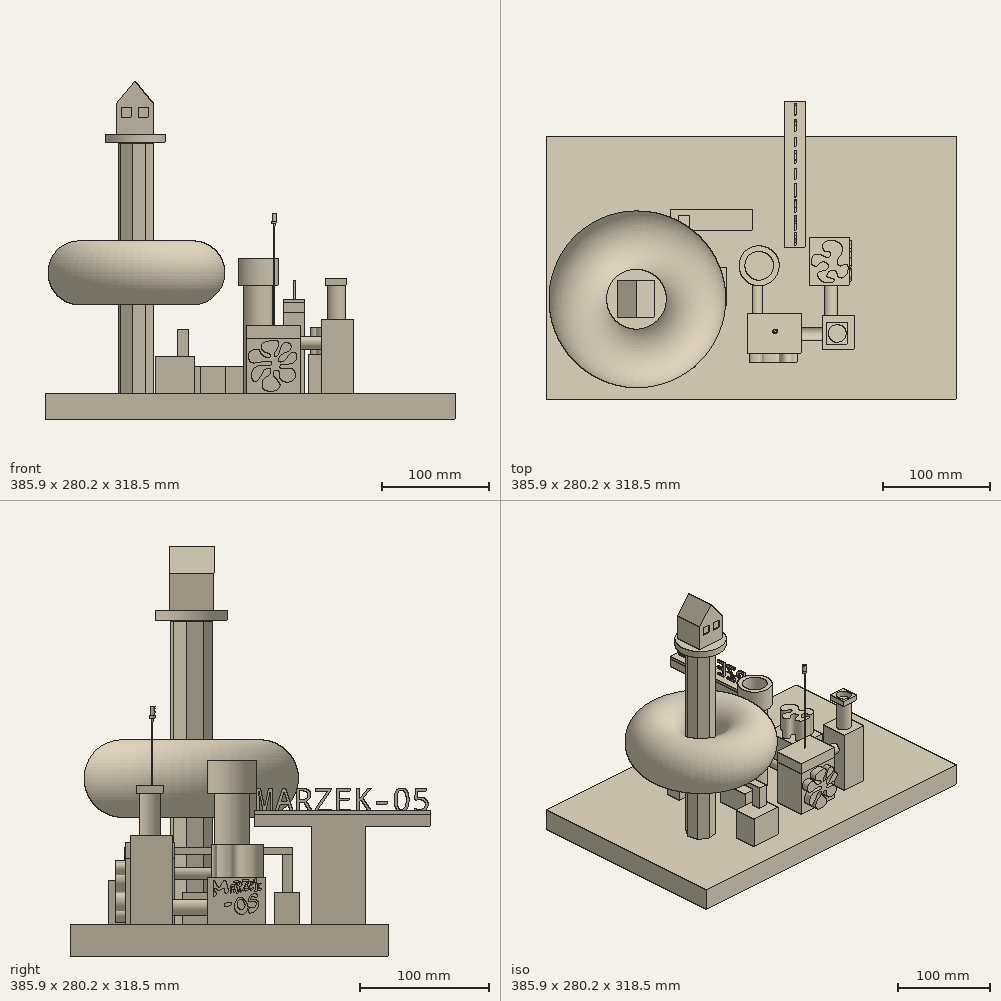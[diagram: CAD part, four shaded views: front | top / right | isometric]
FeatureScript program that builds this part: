
annotation { "Feature Type Name" : "Feature", "Feature Type Description" : "" }
export const myFeature = defineFeature(function(context is Context, id is Id, definition is map)
    precondition{}
    {
        {
            var Q0;
            Q0=qCreatedBy(makeId("Top.planeOp"),FACE);
            var sketch = newSketch(context, id + "F0", { "sketchPlane" : qUnion([Q0])});
            skLineSegment(sketch, "E0.bottom", {"start": v(-130.02, -36.2) * mm, "end": v(-92.83, -36.2) * mm});
            skLineSegment(sketch, "E0.top", {"start": v(-130.02, -64.13) * mm, "end": v(-92.83, -64.13) * mm});
            skLineSegment(sketch, "E0.left", {"start": v(-130.02, -36.2) * mm, "end": v(-130.02, -64.13) * mm});
            skLineSegment(sketch, "E0.right", {"start": v(-92.83, -36.2) * mm, "end": v(-92.83, -64.13) * mm});
            skSolve(sketch);
        }
        {
            var Q0;
            Q0 = qSketchRegion(id + "F0", true);
            extrude(context, id + "F1", {"entities" : qUnion([Q0]), "depth" : 34.54 * mm, "offsetDistance" : 25.4 * mm});
        }
        {
            var Q0;
            Q0=qCreatedBy(makeId("Top.planeOp"),FACE);
            var sketch = newSketch(context, id + "F2", { "sketchPlane" : qUnion([Q0])});
            skLineSegment(sketch, "E1.bottom", {"start": v(-87.23, -7.14) * mm, "end": v(-63.83, -7.14) * mm});
            skLineSegment(sketch, "E1.top", {"start": v(-87.23, 30.34) * mm, "end": v(-63.83, 30.34) * mm});
            skLineSegment(sketch, "E1.left", {"start": v(-87.23, -7.14) * mm, "end": v(-87.23, 30.34) * mm});
            skLineSegment(sketch, "E1.right", {"start": v(-63.83, -7.14) * mm, "end": v(-63.83, 30.34) * mm});
            skSolve(sketch);
        }
        {
            var Q0;
            Q0 = qSketchRegion(id + "F2", true);
            extrude(context, id + "F3", {"entities" : qUnion([Q0]), "depth" : 25.4 * mm, "offsetDistance" : 25.4 * mm});
        }
        {
            var Q0;
            Q0=qCreatedBy(makeId("Top.planeOp"),FACE);
            var sketch = newSketch(context, id + "F4", { "sketchPlane" : qUnion([Q0])});
            skLineSegment(sketch, "E2.bottom", {"start": v(-44.01, -13.42) * mm, "end": v(6.45, -13.42) * mm});
            skLineSegment(sketch, "E2.top", {"start": v(-44.01, -51.12) * mm, "end": v(6.45, -51.12) * mm});
            skLineSegment(sketch, "E2.left", {"start": v(-44.01, -13.42) * mm, "end": v(-44.01, -51.12) * mm});
            skLineSegment(sketch, "E2.right", {"start": v(6.45, -13.42) * mm, "end": v(6.45, -51.12) * mm});
            skSolve(sketch);
        }
        {
            var Q0;
            Q0 = qSketchRegion(id + "F4", true);
            extrude(context, id + "F5", {"entities" : qUnion([Q0]), "depth" : 51.56 * mm, "offsetDistance" : 25.4 * mm});
        }
        {
            var Q0;
            Q0=qCreatedBy(makeId("Top.planeOp"),FACE);
            var sketch = newSketch(context, id + "F6", { "sketchPlane" : qUnion([Q0])});
            skLineSegment(sketch, "E3.bottom", {"start": v(51.77, 57.86) * mm, "end": v(13.62, 57.86) * mm});
            skLineSegment(sketch, "E3.top", {"start": v(51.77, 12.59) * mm, "end": v(13.62, 12.59) * mm});
            skLineSegment(sketch, "E3.left", {"start": v(51.77, 57.86) * mm, "end": v(51.77, 12.59) * mm});
            skLineSegment(sketch, "E3.right", {"start": v(13.62, 57.86) * mm, "end": v(13.62, 12.59) * mm});
            skSolve(sketch);
        }
        {
            var Q0;
            Q0 = qSketchRegion(id + "F6", true);
            extrude(context, id + "F7", {"entities" : qUnion([Q0]), "depth" : 36.58 * mm, "offsetDistance" : 25.4 * mm});
        }
        {
            var Q0;
            Q0=qCreatedBy(makeId("Top.planeOp"),FACE);
            var sketch = newSketch(context, id + "F8", { "sketchPlane" : qUnion([Q0])});
            skLineSegment(sketch, "E4.bottom", {"start": v(-116.39, 64.97) * mm, "end": v(-39.84, 64.97) * mm});
            skLineSegment(sketch, "E4.top", {"start": v(-116.39, 84.23) * mm, "end": v(-39.84, 84.23) * mm});
            skLineSegment(sketch, "E4.left", {"start": v(-116.39, 64.97) * mm, "end": v(-116.39, 84.23) * mm});
            skLineSegment(sketch, "E4.right", {"start": v(-39.84, 64.97) * mm, "end": v(-39.84, 84.23) * mm});
            skSolve(sketch);
        }
        {
            var Q0;
            Q0 = qSketchRegion(id + "F8", true);
            extrude(context, id + "F9", {"entities" : qUnion([Q0]), "depth" : 25.4 * mm, "offsetDistance" : 25.4 * mm});
        }
        {
            var Q0;
            Q0=qCreatedBy(makeId("Top.planeOp"),FACE);
            var sketch = newSketch(context, id + "F10", { "sketchPlane" : qUnion([Q0])});
            skCircle(sketch, "E5", {"center": v(-33.26, 31.48) * mm, "radius": 13.51 * mm});
            skSolve(sketch);
        }
        {
            var Q0;
            Q0 = qSketchRegion(id + "F10", true);
            extrude(context, id + "F11", {"entities" : qUnion([Q0]), "depth" : 101.85 * mm, "offsetDistance" : 25.4 * mm});
        }
        {
            var Q0;
            Q0=qCreatedBy(makeId("Top.planeOp"),FACE);
            var sketch = newSketch(context, id + "F12", { "sketchPlane" : qUnion([Q0])});
            skLineSegment(sketch, "E6.bottom", {"start": v(56.17, -47.26) * mm, "end": v(26.64, -47.26) * mm});
            skLineSegment(sketch, "E6.top", {"start": v(56.17, -14.92) * mm, "end": v(26.64, -14.92) * mm});
            skLineSegment(sketch, "E6.left", {"start": v(56.17, -47.26) * mm, "end": v(56.17, -14.92) * mm});
            skLineSegment(sketch, "E6.right", {"start": v(26.64, -47.26) * mm, "end": v(26.64, -14.92) * mm});
            skSolve(sketch);
        }
        {
            var Q0;
            Q0 = qSketchRegion(id + "F12", true);
            extrude(context, id + "F13", {"entities" : qUnion([Q0]), "depth" : 69.6 * mm, "offsetDistance" : 25.4 * mm});
        }
        {
            var Q0;
            Q0=makeQuery(id+"F13.opExtrude","SWEPT_FACE",FACE,{"disambiguationData":[OSD([sQuery(id+"F12.wireOp",EDGE,"E6.top")])]});
            var sketch = newSketch(context, id + "F14", { "sketchPlane" : qUnion([Q0])});
            skCircle(sketch, "E7", {"center": v(-34.44, 13.3) * mm, "radius": 6.1 * mm});
            skSolve(sketch);
        }
        {
            var Q0;
            Q0 = qSketchRegion(id + "F14", true);
            extrude(context, id + "F15", {"entities" : qUnion([Q0]), "depth" : 30.99 * mm, "offsetDistance" : 25.4 * mm});
        }
        {
            var Q0;
            Q0=makeQuery(id+"F13.opExtrude","SWEPT_FACE",FACE,{"disambiguationData":[OSD([sQuery(id+"F12.wireOp",EDGE,"E6.right")])]});
            var sketch = newSketch(context, id + "F16", { "sketchPlane" : qUnion([Q0])});
            skCircle(sketch, "E8", {"center": v(32.58, 47.44) * mm, "radius": 6.12 * mm});
            skSolve(sketch);
        }
        {
            var Q0;
            Q0 = qSketchRegion(id + "F16", true);
            extrude(context, id + "F17", {"entities" : qUnion([Q0]), "depth" : 25.4 * mm, "offsetDistance" : 25.4 * mm});
        }
        {
            var Q0;
            Q0=makeQuery(id+"F5.opExtrude","CAP_FACE",FACE,{"disambiguationData":[OSD([sQuery(id+"F4.wireOp",EDGE,"E2.bottom"),sQuery(id+"F4.wireOp",EDGE,"E2.top"),sQuery(id+"F4.wireOp",EDGE,"E2.left"),sQuery(id+"F4.wireOp",EDGE,"E2.right")])],"isStart":false});
            extrude(context, id + "F18", {"entities" : qUnion([Q0]), "depth" : 12.7 * mm, "offsetDistance" : 25.4 * mm});
        }
        {
            var Q0;
            Q0=makeQuery(id+"F5.opExtrude","SWEPT_FACE",FACE,{"disambiguationData":[OSD([sQuery(id+"F4.wireOp",EDGE,"E2.bottom")])]});
            var sketch = newSketch(context, id + "F19", { "sketchPlane" : qUnion([Q0])});
            skCircle(sketch, "E9", {"center": v(35.14, 39.92) * mm, "radius": 4.9 * mm});
            skSolve(sketch);
        }
        {
            var Q0;
            Q0 = qSketchRegion(id + "F19", true);
            extrude(context, id + "F20", {"entities" : qUnion([Q0]), "depth" : 37.85 * mm, "offsetDistance" : 25.4 * mm});
        }
        {
            var Q0;
            Q0=makeQuery(id+"F1.opExtrude","CAP_FACE",FACE,{"disambiguationData":[OSD([sQuery(id+"F0.wireOp",EDGE,"E0.bottom"),sQuery(id+"F0.wireOp",EDGE,"E0.top"),sQuery(id+"F0.wireOp",EDGE,"E0.left"),sQuery(id+"F0.wireOp",EDGE,"E0.right")])],"isStart":false});
            var sketch = newSketch(context, id + "F21", { "sketchPlane" : qUnion([Q0])});
            skLineSegment(sketch, "E10.bottom", {"start": v(-98.59, -40.36) * mm, "end": v(-108.85, -40.36) * mm});
            skLineSegment(sketch, "E10.top", {"start": v(-98.59, -51.65) * mm, "end": v(-108.85, -51.65) * mm});
            skLineSegment(sketch, "E10.left", {"start": v(-98.59, -40.36) * mm, "end": v(-98.59, -51.65) * mm});
            skLineSegment(sketch, "E10.right", {"start": v(-108.85, -40.36) * mm, "end": v(-108.85, -51.65) * mm});
            skSolve(sketch);
        }
        {
            var Q0;
            Q0 = qSketchRegion(id + "F21", true);
            extrude(context, id + "F22", {"entities" : qUnion([Q0]), "operationType" : NewBodyOperationType.ADD, "depth" : 25.4 * mm, "offsetDistance" : 25.4 * mm});
        }
        {
            var Q0;
            Q0=makeQuery(id+"F22.opExtrude","SWEPT_FACE",FACE,{"disambiguationData":[OSD([sQuery(id+"F21.wireOp",EDGE,"E10.bottom")])]});
            var sketch = newSketch(context, id + "F23", { "sketchPlane" : qUnion([Q0])});
            skLineSegment(sketch, "E11.bottom", {"start": v(108.85, 59.94) * mm, "end": v(98.59, 59.94) * mm});
            skLineSegment(sketch, "E11.top", {"start": v(108.85, 54.75) * mm, "end": v(98.59, 54.75) * mm});
            skLineSegment(sketch, "E11.left", {"start": v(108.85, 59.94) * mm, "end": v(108.85, 54.75) * mm});
            skLineSegment(sketch, "E11.right", {"start": v(98.59, 59.94) * mm, "end": v(98.59, 54.75) * mm});
            skSolve(sketch);
        }
        {
            var Q0;
            Q0 = qSketchRegion(id + "F23", true);
            extrude(context, id + "F24", {"entities" : qUnion([Q0]), "operationType" : NewBodyOperationType.ADD, "depth" : 118.87 * mm, "offsetDistance" : 25.4 * mm});
        }
        {
            var Q0;
            Q0=makeQuery(id+"F24.opExtrude","SWEPT_FACE",FACE,{"disambiguationData":[OSD([sQuery(id+"F23.wireOp",EDGE,"E11.top")])]});
            var sketch = newSketch(context, id + "F25", { "sketchPlane" : qUnion([Q0])});
            skLineSegment(sketch, "E12.bottom", {"start": v(-108.85, -78.51) * mm, "end": v(-98.59, -78.51) * mm});
            skLineSegment(sketch, "E12.top", {"start": v(-108.85, -71.06) * mm, "end": v(-98.59, -71.06) * mm});
            skLineSegment(sketch, "E12.left", {"start": v(-108.85, -78.51) * mm, "end": v(-108.85, -71.06) * mm});
            skLineSegment(sketch, "E12.right", {"start": v(-98.59, -78.51) * mm, "end": v(-98.59, -71.06) * mm});
            skSolve(sketch);
        }
        {
            var Q0;
            Q0 = qSketchRegion(id + "F25", true);
            extrude(context, id + "F26", {"entities" : qUnion([Q0]), "depth" : 33.78 * mm, "offsetDistance" : 25.4 * mm});
        }
        {
            var Q0;
            Q0=makeQuery(id+"F11.opExtrude","CAP_FACE",FACE,{"disambiguationData":[OSD([sQuery(id+"F10.wireOp",EDGE,"E5")])],"isStart":false});
            var sketch = newSketch(context, id + "F27", { "sketchPlane" : qUnion([Q0])});
            skCircle(sketch, "E13.0", {"center": v(-33.26, 31.48) * mm, "radius": 18.84 * mm});
            skSolve(sketch);
        }
        {
            var Q0;
            Q0=makeQuery(id+"F27.imprint","IMPRINT",FACE,{"disambiguationData":[TD([[makeQuery(id+"F27.imprint","IMPRINT",EDGE,{"derivedFrom":sQuery(id+"F27.wireOp",EDGE,"E13.0")}),1.0]])]});
            extrude(context, id + "F28", {"entities" : qUnion([Q0]), "depth" : 25.4 * mm, "offsetDistance" : 25.4 * mm});
        }
        {
            var Q0;
            Q0=makeQuery(id+"F13.opExtrude","CAP_FACE",FACE,{"disambiguationData":[OSD([sQuery(id+"F12.wireOp",EDGE,"E6.bottom"),sQuery(id+"F12.wireOp",EDGE,"E6.top"),sQuery(id+"F12.wireOp",EDGE,"E6.left"),sQuery(id+"F12.wireOp",EDGE,"E6.right")])],"isStart":false});
            var sketch = newSketch(context, id + "F29", { "sketchPlane" : qUnion([Q0])});
            skCircle(sketch, "E14", {"center": v(40.34, -32.18) * mm, "radius": 8.32 * mm});
            skSolve(sketch);
        }
        {
            var Q0;
            Q0 = qSketchRegion(id + "F29", true);
            extrude(context, id + "F30", {"entities" : qUnion([Q0]), "operationType" : NewBodyOperationType.ADD, "depth" : 25.4 * mm, "offsetDistance" : 25.4 * mm});
        }
        {
            var Q0;
            Q0=makeQuery(id+"F30.opExtrude","CAP_FACE",FACE,{"disambiguationData":[OSD([sQuery(id+"F29.wireOp",EDGE,"E14")])],"isStart":false});
            extrude(context, id + "F31", {"entities" : qUnion([Q0]), "operationType" : NewBodyOperationType.ADD, "depth" : 7.11 * mm, "offsetDistance" : 25.4 * mm});
        }
        {
            var Q0;
            Q0=makeQuery(id+"F31.opExtrude","CAP_FACE",FACE,{"disambiguationData":[OSD([sQuery(id+"F29.wireOp",EDGE,"E14")])],"isStart":false});
            var sketch = newSketch(context, id + "F32", { "sketchPlane" : qUnion([Q0])});
            skLineSegment(sketch, "E15.bottom", {"start": v(50.17, -42.34) * mm, "end": v(30.38, -42.34) * mm});
            skLineSegment(sketch, "E15.top", {"start": v(50.17, -21.75) * mm, "end": v(30.38, -21.75) * mm});
            skLineSegment(sketch, "E15.left", {"start": v(50.17, -42.34) * mm, "end": v(50.17, -21.75) * mm});
            skLineSegment(sketch, "E15.right", {"start": v(30.38, -42.34) * mm, "end": v(30.38, -21.75) * mm});
            skSolve(sketch);
        }
        {
            var Q0;
            Q0=makeQuery(id+"F32.imprint","IMPRINT",FACE,{"disambiguationData":[TD([[makeQuery(id+"F32.imprint","IMPRINT",EDGE,{"derivedFrom":sQuery(id+"F32.wireOp",EDGE,"E15.bottom")}),-1.0]])]});
            extrude(context, id + "F33", {"entities" : qUnion([Q0]), "depth" : 6.43 * mm, "offsetDistance" : 25.4 * mm});
        }
        {
            var Q0;
            Q0=makeQuery(id+"F18.opExtrude","CAP_FACE",FACE,{"disambiguationData":[OSD([sQuery(id+"F4.wireOp",EDGE,"E2.bottom"),sQuery(id+"F4.wireOp",EDGE,"E2.top"),sQuery(id+"F4.wireOp",EDGE,"E2.left"),sQuery(id+"F4.wireOp",EDGE,"E2.right")])],"isStart":false});
            var sketch = newSketch(context, id + "F34", { "sketchPlane" : qUnion([Q0])});
            skCircle(sketch, "E16", {"center": v(-18.17, -30.28) * mm, "radius": 0.48 * mm});
            skSolve(sketch);
        }
        {
            var Q0;
            Q0 = qSketchRegion(id + "F34", true);
            extrude(context, id + "F35", {"entities" : qUnion([Q0]), "operationType" : NewBodyOperationType.ADD, "depth" : 93.22 * mm, "offsetDistance" : 25.4 * mm});
        }
        {
            var Q0;
            Q0=makeQuery(id+"F35.opExtrude","CAP_FACE",FACE,{"disambiguationData":[OSD([sQuery(id+"F34.wireOp",EDGE,"E16")])],"isStart":false});
            var sketch = newSketch(context, id + "F36", { "sketchPlane" : qUnion([Q0])});
            skCircle(sketch, "E17", {"center": v(-18.17, -30.28) * mm, "radius": 0.82 * mm});
            skSolve(sketch);
        }
        {
            var Q0;
            Q0 = qSketchRegion(id + "F36", true);
            extrude(context, id + "F37", {"entities" : qUnion([Q0]), "operationType" : NewBodyOperationType.ADD, "depth" : 2.5 * mm, "offsetDistance" : 25.4 * mm});
        }
        {
            var Q0;
            Q0=makeQuery(id+"F37.opExtrude","CAP_FACE",FACE,{"disambiguationData":[OSD([sQuery(id+"F36.wireOp",EDGE,"E17")])],"isStart":false});
            var sketch = newSketch(context, id + "F38", { "sketchPlane" : qUnion([Q0])});
            skCircle(sketch, "E18", {"center": v(-18.17, -30.28) * mm, "radius": 2.23 * mm});
            skSolve(sketch);
        }
        {
            var Q0;
            Q0 = qSketchRegion(id + "F38", true);
            extrude(context, id + "F39", {"entities" : qUnion([Q0]), "operationType" : NewBodyOperationType.ADD, "depth" : 2.31 * mm, "offsetDistance" : 25.4 * mm});
        }
        {
            var Q0;
            Q0=makeQuery(id+"F39.opExtrude","CAP_FACE",FACE,{"disambiguationData":[OSD([sQuery(id+"F38.wireOp",EDGE,"E18")])],"isStart":false});
            var sketch = newSketch(context, id + "F40", { "sketchPlane" : qUnion([Q0])});
            skFitSpline(sketch, "E19", {"points": [v(-19.47, -28.47) * mm, v(-19.33, -29.35) * mm, v(-17.88, -29.43) * mm, v(-16.97, -30.45) * mm, v(-17.8, -31.58) * mm, v(-18.95, -30.84) * mm, v(-18.93, -30.07) * mm, v(-19.67, -29.84) * mm, v(-20.12, -30.45) * mm, v(-19.86, -31.24) * mm, v(-18.63, -32.03) * mm, v(-17.06, -31.86) * mm, v(-16.48, -30.94) * mm, v(-16.36, -29.54) * mm, v(-17.08, -28.7) * mm, v(-18.31, -29.05) * mm, v(-18.97, -29.18) * mm, v(-19.1, -28.92) * mm, v(-18.7, -28.5) * mm, v(-18.06, -28.44) * mm, v(-17.04, -28.37) * mm, v(-19.47, -28.47) * mm]});
            skSolve(sketch);
        }
        {
            var Q0;
            Q0 = qSketchRegion(id + "F40", true);
            extrude(context, id + "F41", {"entities" : qUnion([Q0]), "operationType" : NewBodyOperationType.ADD, "depth" : 7.11 * mm, "offsetDistance" : 25.4 * mm});
        }
        {
            var Q0;
            Q0=makeQuery(id+"F7.opExtrude","CAP_FACE",FACE,{"disambiguationData":[OSD([sQuery(id+"F6.wireOp",EDGE,"E3.bottom"),sQuery(id+"F6.wireOp",EDGE,"E3.top"),sQuery(id+"F6.wireOp",EDGE,"E3.left"),sQuery(id+"F6.wireOp",EDGE,"E3.right")])],"isStart":false});
            var sketch = newSketch(context, id + "F42", { "sketchPlane" : qUnion([Q0])});
            skFitSpline(sketch, "E20", {"points": [v(32.91, 15.98) * mm, v(29.48, 15.98) * mm, v(25.94, 16.9) * mm, v(22.86, 19.93) * mm, v(21.8, 22.74) * mm, v(22.9, 25.61) * mm, v(26.5, 26.67) * mm, v(30.48, 27.84) * mm, v(31.72, 31.1) * mm, v(30.42, 34.2) * mm, v(26.63, 35.13) * mm, v(22.86, 32.62) * mm, v(20.15, 31.14) * mm, v(16.14, 33.14) * mm, v(16, 37.11) * mm, v(19.33, 41.88) * mm, v(24.05, 42.23) * mm, v(27.94, 40.37) * mm, v(32.1, 39.55) * mm, v(33.97, 42.13) * mm, v(32.39, 44.57) * mm, v(30.24, 44.91) * mm, v(27.6, 46.07) * mm, v(26.46, 50.21) * mm, v(30.41, 54.7) * mm, v(38.06, 55.2) * mm, v(43.42, 51.7) * mm, v(45.1, 48.46) * mm, v(43.88, 41.76) * mm, v(41.76, 38.93) * mm, v(40.02, 36.09) * mm, v(41.05, 32.6) * mm, v(44.45, 31.42) * mm, v(46.66, 32.8) * mm, v(49.7, 32.29) * mm, v(50.49, 29.08) * mm, v(49.44, 23.96) * mm, v(45.25, 20.15) * mm, v(40.97, 21.5) * mm, v(39.44, 25.53) * mm, v(34.27, 27.04) * mm, v(30.54, 21.5) * mm, v(33.93, 20.04) * mm, v(36.94, 18.87) * mm, v(36.87, 16.5) * mm, v(32.91, 15.98) * mm]});
            skSolve(sketch);
        }
        {
            var Q0;
            Q0 = qSketchRegion(id + "F42", true);
            extrude(context, id + "F43", {"entities" : qUnion([Q0]), "operationType" : NewBodyOperationType.ADD, "depth" : 25.4 * mm, "offsetDistance" : 25.4 * mm});
        }
        {
            var Q0;
            Q0=makeQuery(id+"F9.opExtrude","SWEPT_FACE",FACE,{"disambiguationData":[OSD([sQuery(id+"F8.wireOp",EDGE,"E4.top")])]});
            var sketch = newSketch(context, id + "F44", { "sketchPlane" : qUnion([Q0])});
            skFitSpline(sketch, "E21", {"points": [v(78.26, 24.17) * mm, v(70.84, 24.1) * mm, v(61.58, 23.05) * mm, v(55.83, 21.14) * mm, v(50.49, 17.55) * mm, v(48.41, 14.91) * mm, v(47.7, 12.04) * mm, v(47.7, 9.4) * mm, v(48.97, 6.06) * mm, v(53.2, 3.34) * mm, v(59.42, 1.9) * mm, v(68.12, 1.35) * mm, v(76.98, 1.35) * mm, v(86.56, 1.67) * mm, v(97.17, 3.1) * mm, v(102.92, 5.66) * mm, v(107.23, 9.57) * mm, v(107.3, 11.24) * mm, v(106.27, 12.12) * mm, v(104.2, 11.16) * mm, v(100.28, 8.69) * mm, v(93.58, 7.5) * mm, v(83.2, 8.37) * mm, v(78.5, 11.4) * mm, v(77.86, 15.71) * mm, v(82, 18.82) * mm, v(90.7, 19.46) * mm, v(98.05, 16.9) * mm, v(100.52, 14.12) * mm, v(102.6, 13.56) * mm, v(104.11, 15.95) * mm, v(102.28, 18.98) * mm, v(95.18, 22.41) * mm, v(83.36, 24.17) * mm, v(78.26, 24.17) * mm]});
            skSolve(sketch);
        }
        {
            var Q0;
            Q0 = qSketchRegion(id + "F44", true);
            extrude(context, id + "F45", {"entities" : qUnion([Q0]), "operationType" : NewBodyOperationType.REMOVE, "oppositeDirection" : true, "depth" : 6.35 * mm, "offsetDistance" : 25.4 * mm});
        }
        {
            var Q0;
            Q0=makeQuery(id+"F5.opExtrude","SWEPT_FACE",FACE,{"disambiguationData":[OSD([sQuery(id+"F4.wireOp",EDGE,"E2.top")])]});
            var sketch = newSketch(context, id + "F46", { "sketchPlane" : qUnion([Q0])});
            skFitSpline(sketch, "E22", {"points": [v(-18.89, 49.93) * mm, v(-16.42, 49.93) * mm, v(-14.33, 48.79) * mm, v(-13.76, 46.6) * mm, v(-14.8, 42.8) * mm, v(-17.18, 38.92) * mm, v(-18.03, 36.83) * mm, v(-17.27, 34.74) * mm, v(-14.8, 35.7) * mm, v(-13.1, 39.87) * mm, v(-11.96, 43.1) * mm, v(-9.4, 46.89) * mm, v(-6.65, 47.84) * mm, v(-3.32, 46.7) * mm, v(-2.1, 43.57) * mm, v(-4.18, 40.06) * mm, v(-8.45, 37.97) * mm, v(-11.96, 35.4) * mm, v(-13.57, 33.41) * mm, v(-13.95, 31.32) * mm, v(-13.2, 30) * mm, v(-9.5, 30) * mm, v(-6.46, 32.75) * mm, v(-4.08, 35.98) * mm, v(-1.52, 38.16) * mm, v(1.52, 38.16) * mm, v(2.94, 35.7) * mm, v(2.75, 31.7) * mm, v(0, 28.95) * mm, v(-3.23, 27.9) * mm, v(-7.31, 27.43) * mm, v(-11.58, 27.05) * mm, v(-12.62, 25.73) * mm, v(-12.81, 24.4) * mm, v(-10.63, 23.54) * mm, v(-7.12, 23.73) * mm, v(-2.38, 23.45) * mm, v(0.85, 20.98) * mm, v(1.7, 15.29) * mm, v(-1.14, 11.68) * mm, v(-7.6, 10.83) * mm, v(-12.25, 13.48) * mm, v(-13.1, 17.66) * mm, v(-13.38, 20.5) * mm, v(-15.66, 21.93) * mm, v(-17.65, 21.55) * mm, v(-18.98, 18.99) * mm, v(-18.7, 16.8) * mm, v(-15.95, 13.2) * mm, v(-12.81, 8.74) * mm, v(-13.67, 4.85) * mm, v(-19.17, 2.2) * mm, v(-27.9, 3.9) * mm, v(-29.52, 9.78) * mm, v(-26.67, 14.53) * mm, v(-23.06, 17.18) * mm, v(-21.55, 19.94) * mm, v(-22.3, 23.54) * mm, v(-24.77, 23.45) * mm, v(-27.14, 22.12) * mm, v(-30.18, 16.9) * mm, v(-35.78, 11.2) * mm, v(-38.82, 13.39) * mm, v(-39.48, 18.13) * mm, v(-36.63, 23.83) * mm, v(-30.66, 26.4) * mm, v(-25.91, 26.1) * mm, v(-22.5, 26.2) * mm, v(-20.5, 27.53) * mm, v(-20.79, 29.71) * mm, v(-26.86, 30.28) * mm, v(-33.79, 28.95) * mm, v(-39.39, 29.14) * mm, v(-41.66, 31.6) * mm, v(-42.42, 35.7) * mm, v(-40.72, 39.49) * mm, v(-32.74, 41.1) * mm, v(-30.66, 37.78) * mm, v(-25.53, 33.89) * mm, v(-21.93, 33.98) * mm, v(-21.83, 35.98) * mm, v(-25.44, 38.44) * mm, v(-29.42, 40.72) * mm, v(-30.09, 45.94) * mm, v(-24.96, 48.88) * mm, v(-18.89, 49.93) * mm]});
            skSolve(sketch);
        }
        {
            var Q0;
            Q0 = qSketchRegion(id + "F46", true);
            extrude(context, id + "F47", {"entities" : qUnion([Q0]), "operationType" : NewBodyOperationType.ADD, "depth" : 7.87 * mm, "offsetDistance" : 25.4 * mm});
        }
        {
            var Q0;
            Q0=makeQuery(id+"F7.opExtrude","SWEPT_FACE",FACE,{"disambiguationData":[OSD([sQuery(id+"F6.wireOp",EDGE,"E3.left")])]});
            var sketch = newSketch(context, id + "F48", { "sketchPlane" : qUnion([Q0])});
            skFitSpline(sketch, "E23", {"points": [v(16.83, 25.89) * mm, v(17.83, 34.59) * mm, v(21.64, 29.04) * mm, v(25.87, 34.49) * mm, v(28.57, 25.33) * mm, v(27.44, 24.5) * mm, v(25.74, 25.97) * mm, v(25.68, 28.52) * mm, v(22.86, 26.97) * mm, v(20.46, 26.83) * mm, v(18.46, 28.59) * mm, v(18.09, 26.81) * mm, v(19.51, 24) * mm, v(17.65, 21.93) * mm, v(16.83, 25.89) * mm]});
            skFitSpline(sketch, "E24", {"points": [v(30.3, 25.33) * mm, v(30.23, 27.42) * mm, v(30.48, 29.91) * mm, v(31.53, 31.23) * mm, v(33.19, 31.06) * mm, v(33.6, 29.68) * mm, v(33.91, 27.15) * mm, v(33.81, 25.33) * mm, v(32.95, 25.33) * mm, v(32.81, 26.6) * mm, v(32.29, 27.45) * mm, v(31.32, 27.22) * mm, v(31.35, 25.89) * mm, v(30.93, 24.34) * mm, v(30.3, 25.33) * mm]});
            skFitSpline(sketch, "E25", {"points": [v(32.24, 30.06) * mm, v(31.66, 29.95) * mm, v(31.27, 29.27) * mm, v(31.33, 28.52) * mm, v(32.18, 28.52) * mm, v(32.67, 29.04) * mm, v(32.24, 30.06) * mm]});
            skFitSpline(sketch, "E26", {"points": [v(35.2, 24.26) * mm, v(35.8, 25.89) * mm, v(35.82, 27.42) * mm, v(34.85, 30.79) * mm, v(33.91, 32.57) * mm, v(32.18, 32.87) * mm, v(33.6, 33.87) * mm, v(36.64, 33.97) * mm, v(39.25, 32) * mm, v(38.75, 30.06) * mm, v(37.02, 29.68) * mm, v(38.21, 27.42) * mm, v(38.96, 26.4) * mm, v(40.3, 25.89) * mm, v(38.88, 25.33) * mm, v(38.04, 25.33) * mm, v(36.62, 28.52) * mm, v(36.44, 27.95) * mm, v(36.74, 25.89) * mm, v(36.7, 24.33) * mm, v(35.2, 24.26) * mm]});
            skFitSpline(sketch, "E27", {"points": [v(35.52, 33.09) * mm, v(36.51, 33.1) * mm, v(37.44, 32.54) * mm, v(37.72, 31.95) * mm, v(37.3, 31.1) * mm, v(35.98, 30.82) * mm, v(35.52, 33.09) * mm]});
            skFitSpline(sketch, "E28", {"points": [v(39.57, 34.57) * mm, v(39.72, 32.94) * mm, v(40.54, 33.27) * mm, v(43.3, 33.78) * mm, v(42.8, 32.42) * mm, v(40.93, 28.74) * mm, v(40.13, 26.8) * mm, v(41.28, 26.35) * mm, v(43.82, 26.6) * mm, v(44.05, 28.16) * mm, v(41.18, 27.53) * mm, v(44.35, 33.59) * mm, v(44.11, 35.09) * mm, v(39.57, 34.57) * mm]});
            skFitSpline(sketch, "E29", {"points": [v(45.78, 30.79) * mm, v(46.85, 30.79) * mm, v(48.2, 31.28) * mm, v(48.07, 33.29) * mm, v(45.86, 33.45) * mm, v(44.1, 31.5) * mm, v(44.04, 29.68) * mm, v(45.37, 27.34) * mm, v(47.15, 26.76) * mm, v(48.47, 27.83) * mm, v(48.34, 29.11) * mm, v(47.3, 28.63) * mm, v(46.52, 28.04) * mm, v(45.25, 28.86) * mm, v(45.78, 30.79) * mm]});
            skFitSpline(sketch, "E30", {"points": [v(45.5, 32.08) * mm, v(46, 32.65) * mm, v(46.91, 32.9) * mm, v(47.53, 32.29) * mm, v(47.33, 31.77) * mm, v(46.45, 31.56) * mm, v(45.78, 31.62) * mm, v(45.5, 32.08) * mm]});
            skFitSpline(sketch, "E31", {"points": [v(49.06, 35.24) * mm, v(49.77, 35.76) * mm, v(50.54, 35.76) * mm, v(51.23, 29.28) * mm, v(51.88, 30.23) * mm, v(52.72, 32.08) * mm, v(53.4, 32.08) * mm, v(54.44, 32.08) * mm, v(53.82, 31.07) * mm, v(52.4, 29.68) * mm, v(52.77, 28.9) * mm, v(54.16, 28.16) * mm, v(54.93, 27.47) * mm, v(53.6, 26.85) * mm, v(52.5, 26.82) * mm, v(52.37, 27.67) * mm, v(51.92, 28.74) * mm, v(51.43, 28.73) * mm, v(51.72, 26.59) * mm, v(49.2, 25.89) * mm, v(49.65, 26.97) * mm, v(49.64, 28.79) * mm, v(49.16, 33.88) * mm, v(48.29, 34.57) * mm, v(49.06, 35.24) * mm]});
            skSolve(sketch);
        }
        {
            var Q0;
            Q0=makeQuery(id+"F48.imprint","IMPRINT",FACE,{"disambiguationData":[TD([[makeQuery(id+"F48.imprint","IMPRINT",EDGE,{"derivedFrom":sQuery(id+"F48.wireOp",EDGE,"E23")}),-1.0]])]});
            var Q1;
            Q1=makeQuery(id+"F48.imprint","IMPRINT",FACE,{"disambiguationData":[TD([[makeQuery(id+"F48.imprint","IMPRINT",EDGE,{"derivedFrom":sQuery(id+"F48.wireOp",EDGE,"E24")}),-1.0]])]});
            var Q2;
            Q2=makeQuery(id+"F48.imprint","IMPRINT",FACE,{"disambiguationData":[TD([[makeQuery(id+"F48.imprint","IMPRINT",EDGE,{"derivedFrom":sQuery(id+"F48.wireOp",EDGE,"E26")}),-1.0]])]});
            var Q3;
            Q3=makeQuery(id+"F48.imprint","IMPRINT",FACE,{"disambiguationData":[TD([[makeQuery(id+"F48.imprint","IMPRINT",EDGE,{"derivedFrom":sQuery(id+"F48.wireOp",EDGE,"E28")}),1.0]])]});
            var Q4;
            Q4=makeQuery(id+"F48.imprint","IMPRINT",FACE,{"disambiguationData":[TD([[makeQuery(id+"F48.imprint","IMPRINT",EDGE,{"derivedFrom":sQuery(id+"F48.wireOp",EDGE,"E29")}),1.0]])]});
            var Q5;
            Q5=makeQuery(id+"F48.imprint","IMPRINT",FACE,{"disambiguationData":[TD([[makeQuery(id+"F48.imprint","IMPRINT",EDGE,{"derivedFrom":sQuery(id+"F48.wireOp",EDGE,"E31")}),-1.0]])]});
            extrude(context, id + "F49", {"entities" : qUnion([Q0, Q1, Q2, Q3, Q4, Q5]), "operationType" : NewBodyOperationType.ADD, "depth" : 1.45 * mm, "offsetDistance" : 25.4 * mm});
        }
        {
            var Q0;
            {var subQ2=sQuery(id+"F6.wireOp",EDGE,"E3.left");var subQ3=sQuery(id+"F6.wireOp",EDGE,"E3.bottom");Q0=makeQuery(id+"F49.boolean.opBoolean","SPLIT",FACE,{"disambiguationData":[TD([makeQuery(id+"F7.opExtrude","SWEPT_FACE",FACE,{"disambiguationData":[OSD([subQ3])]})])],"derivedFrom":makeQuery(id+"F7.opExtrude","SWEPT_FACE",FACE,{"disambiguationData":[OSD([subQ2])]})});}
            var sketch = newSketch(context, id + "F50", { "sketchPlane" : qUnion([Q0])});
            skFitSpline(sketch, "E32", {"points": [v(30.02, 17.28) * mm, v(28.13, 17.02) * mm, v(25.96, 16.59) * mm, v(25.42, 15.64) * mm, v(25.51, 14.56) * mm, v(26.47, 14.18) * mm, v(30.31, 14.83) * mm, v(31.53, 15.97) * mm, v(31.32, 16.78) * mm, v(30.02, 17.28) * mm]});
            skFitSpline(sketch, "E33", {"points": [v(38.44, 21.39) * mm, v(36.43, 20.61) * mm, v(34.84, 18.57) * mm, v(33.64, 15.55) * mm, v(33.8, 12.36) * mm, v(36.06, 9.08) * mm, v(40.9, 8.27) * mm, v(43.7, 11.4) * mm, v(43.63, 15.95) * mm, v(40.8, 19.82) * mm, v(38.44, 21.39) * mm]});
            skFitSpline(sketch, "E34", {"points": [v(38.44, 19.74) * mm, v(36.96, 18.77) * mm, v(35.65, 16.32) * mm, v(36, 13.86) * mm, v(37.9, 12.2) * mm, v(40.4, 12.04) * mm, v(41.77, 14.38) * mm, v(41.14, 17.28) * mm, v(39.53, 19.13) * mm, v(38.44, 19.74) * mm]});
            skFitSpline(sketch, "E35", {"points": [v(45.7, 22.18) * mm, v(45.04, 17.89) * mm, v(46.93, 18.1) * mm, v(48.88, 18.36) * mm, v(50.4, 17.28) * mm, v(50.46, 15.11) * mm, v(48.25, 13.15) * mm, v(45.51, 13.26) * mm, v(44.86, 9.6) * mm, v(47.65, 9.31) * mm, v(50.37, 10.97) * mm, v(52.21, 14.42) * mm, v(51.72, 17.96) * mm, v(49.81, 19.52) * mm, v(46.4, 19.48) * mm, v(46.54, 21.39) * mm, v(46.96, 21.96) * mm, v(50.89, 21.39) * mm, v(51.47, 22.01) * mm, v(50.88, 23.97) * mm, v(45.7, 22.18) * mm]});
            skSolve(sketch);
        }
        {
            var Q0;
            Q0=makeQuery(id+"F50.imprint","IMPRINT",FACE,{"disambiguationData":[TD([[makeQuery(id+"F50.imprint","IMPRINT",EDGE,{"derivedFrom":sQuery(id+"F50.wireOp",EDGE,"E32")}),1.0]])]});
            var Q1;
            Q1=makeQuery(id+"F50.imprint","IMPRINT",FACE,{"disambiguationData":[TD([[makeQuery(id+"F50.imprint","IMPRINT",EDGE,{"derivedFrom":sQuery(id+"F50.wireOp",EDGE,"E33")}),1.0]])]});
            var Q2;
            Q2=makeQuery(id+"F50.imprint","IMPRINT",FACE,{"disambiguationData":[TD([[makeQuery(id+"F50.imprint","IMPRINT",EDGE,{"derivedFrom":sQuery(id+"F50.wireOp",EDGE,"E35")}),1.0]])]});
            extrude(context, id + "F51", {"entities" : qUnion([Q0, Q1, Q2]), "operationType" : NewBodyOperationType.ADD, "depth" : 0.76 * mm, "offsetDistance" : 25.4 * mm});
        }
        {
            var Q0;
            Q0=qCreatedBy(makeId("Right.planeOp"),FACE);
            var sketch = newSketch(context, id + "F52", { "sketchPlane" : qUnion([Q0])});
            skText(sketch, "E36", { "text": "MARZEK-05", "fontName": "DroidSansMono.ttf"});
            const initialGuessF52  = {"E36": [0.04935, 0.08785, 1, 0, 0.01824]};
            skSetInitialGuess(sketch, initialGuessF52);
            skSolve(sketch);
        }
        {
            var Q0;
            Q0 = qSketchRegion(id + "F52", true);
            extrude(context, id + "F53", {"entities" : qUnion([Q0]), "depth" : 2.03 * mm, "offsetDistance" : 25.4 * mm});
        }
        {
            var Q0;
            Q0=qCreatedBy(makeId("Right.planeOp"),FACE);
            var sketch = newSketch(context, id + "F54", { "sketchPlane" : qUnion([Q0])});
            skLineSegment(sketch, "E37.bottom", {"start": v(186.06, 76.14) * mm, "end": v(48.92, 76.14) * mm});
            skLineSegment(sketch, "E37.top", {"start": v(186.06, 85.8) * mm, "end": v(48.92, 85.8) * mm});
            skLineSegment(sketch, "E37.left", {"start": v(186.06, 76.14) * mm, "end": v(186.06, 85.8) * mm});
            skLineSegment(sketch, "E37.right", {"start": v(48.92, 76.14) * mm, "end": v(48.92, 85.8) * mm});
            skSolve(sketch);
        }
        {
            var Q0;
            Q0 = qSketchRegion(id + "F54", true);
            extrude(context, id + "F55", {"entities" : qUnion([Q0]), "depth" : 10.67 * mm, "offsetDistance" : 25.4 * mm});
        }
        {
            var Q0;
            Q0=makeQuery(id+"F55.opExtrude","CAP_FACE",FACE,{"disambiguationData":[OSD([sQuery(id+"F54.wireOp",EDGE,"E37.bottom"),sQuery(id+"F54.wireOp",EDGE,"E37.top"),sQuery(id+"F54.wireOp",EDGE,"E37.left"),sQuery(id+"F54.wireOp",EDGE,"E37.right")])],"isStart":true});
            extrude(context, id + "F56", {"entities" : qUnion([Q0]), "operationType" : NewBodyOperationType.ADD, "depth" : 9.65 * mm, "offsetDistance" : 25.4 * mm});
        }
        {
            var Q0;
            {var subQ0=sQuery(id+"F54.wireOp",EDGE,"E37.top");Q0=makeQuery(id+"F56.boolean.opBoolean","MERGE",FACE,{"derivedFrom":[makeQuery(id+"F55.opExtrude","SWEPT_FACE",FACE,{"disambiguationData":[OSD([subQ0])]}),makeQuery(id+"F56.opExtrude","SWEPT_FACE",FACE,{"disambiguationData":[OSD([subQ0])]})]});}
            extrude(context, id + "F57", {"entities" : qUnion([Q0]), "depth" : 2.8 * mm, "offsetDistance" : 25.4 * mm});
        }
        {
            var Q0;
            {var subQ0=sQuery(id+"F54.wireOp",EDGE,"E37.bottom");Q0=makeQuery(id+"F56.boolean.opBoolean","MERGE",FACE,{"derivedFrom":[makeQuery(id+"F55.opExtrude","SWEPT_FACE",FACE,{"disambiguationData":[OSD([subQ0])]}),makeQuery(id+"F56.opExtrude","SWEPT_FACE",FACE,{"disambiguationData":[OSD([subQ0])]})]});}
            var sketch = newSketch(context, id + "F58", { "sketchPlane" : qUnion([Q0])});
            skLineSegment(sketch, "E38.bottom", {"start": v(10.67, -93.69) * mm, "end": v(-9.65, -93.69) * mm});
            skLineSegment(sketch, "E38.top", {"start": v(10.67, -135.25) * mm, "end": v(-9.65, -135.25) * mm});
            skLineSegment(sketch, "E38.left", {"start": v(10.67, -93.69) * mm, "end": v(10.67, -135.25) * mm});
            skLineSegment(sketch, "E38.right", {"start": v(-9.65, -93.69) * mm, "end": v(-9.65, -135.25) * mm});
            skSolve(sketch);
        }
        {
            var Q0;
            Q0=makeQuery(id+"F58.imprint","IMPRINT",FACE,{"disambiguationData":[TD([[makeQuery(id+"F58.imprint","IMPRINT",EDGE,{"derivedFrom":sQuery(id+"F58.wireOp",EDGE,"E38.bottom")}),1.0]])]});
            extrude(context, id + "F59", {"entities" : qUnion([Q0]), "operationType" : NewBodyOperationType.ADD, "depth" : 76.2 * mm, "offsetDistance" : 25.4 * mm});
        }
        {
            var Q0;
            Q0=qCreatedBy(makeId("Top.planeOp"),FACE);
            var sketch = newSketch(context, id + "F60", { "sketchPlane" : qUnion([Q0])});
            skLineSegment(sketch, "E39.bottom", {"start": v(152.42, 153.48) * mm, "end": v(-100.97, 153.48) * mm});
            skLineSegment(sketch, "E39.top", {"start": v(152.42, -94.16) * mm, "end": v(-100.97, -94.16) * mm});
            skLineSegment(sketch, "E39.left", {"start": v(152.42, 153.48) * mm, "end": v(152.42, -94.16) * mm});
            skLineSegment(sketch, "E39.right", {"start": v(-100.97, 153.48) * mm, "end": v(-100.97, -94.16) * mm});
            skLineSegment(sketch, "E40.bottom", {"start": v(-100.97, -94.16) * mm, "end": v(-233.46, -94.16) * mm});
            skLineSegment(sketch, "E40.top", {"start": v(-100.97, 153.48) * mm, "end": v(-233.46, 153.48) * mm});
            skLineSegment(sketch, "E40.left", {"start": v(-100.97, -94.16) * mm, "end": v(-100.97, 153.48) * mm});
            skLineSegment(sketch, "E40.right", {"start": v(-233.46, -94.16) * mm, "end": v(-233.46, 153.48) * mm});
            skSolve(sketch);
        }
        {
            var Q0;
            Q0=makeQuery(id+"F60.imprint","IMPRINT",FACE,{"disambiguationData":[TD([[makeQuery(id+"F60.imprint","IMPRINT",EDGE,{"derivedFrom":sQuery(id+"F60.wireOp",EDGE,"E40.bottom")}),-1.0]])]});
            var Q1;
            Q1=makeQuery(id+"F60.imprint","IMPRINT",FACE,{"disambiguationData":[TD([[makeQuery(id+"F60.imprint","IMPRINT",EDGE,{"derivedFrom":sQuery(id+"F60.wireOp",EDGE,"E39.bottom")}),1.0]])]});
            extrude(context, id + "F61", {"entities" : qUnion([Q0, Q1]), "oppositeDirection" : true, "depth" : 24.64 * mm, "offsetDistance" : 25.4 * mm});
        }
        {
            var Q0;
            Q0=qCreatedBy(makeId("Front.planeOp"),FACE);
            var sketch = newSketch(context, id + "F62", { "sketchPlane" : qUnion([Q0])});
            skCircle(sketch, "E41", {"center": v(-94.82, 113.56) * mm, "radius": 30.16 * mm});
            skLineSegment(sketch, "E42", {"start": v(-147.9, 133.46) * mm, "end": v(-147.9, 100.64) * mm});
            skSolve(sketch);
        }
        {
            var Q0;
            Q0=makeQuery(id+"F62.imprint","IMPRINT",FACE,{"disambiguationData":[TD([[makeQuery(id+"F62.imprint","IMPRINT",EDGE,{"derivedFrom":sQuery(id+"F62.wireOp",EDGE,"E41")}),1.0]])]});
            var Q1;
            Q1=sQuery(id+"F62.wireOp",EDGE,"E42");
            revolve(context, id + "F63", {"surfaceOperationType" : NewSurfaceOperationType.NEW, "entities" : qUnion([Q0]), "axis" : qUnion([Q1]), "revolveType" : RevolveType.FULL});
        }
        {
            var Q0;
            Q0=makeQuery(id+"F61.opExtrude","CAP_FACE",FACE,{"disambiguationData":[OSD([sQuery(id+"F60.wireOp",EDGE,"E39.bottom"),sQuery(id+"F60.wireOp",EDGE,"E39.top"),sQuery(id+"F60.wireOp",EDGE,"E39.left"),sQuery(id+"F60.wireOp",EDGE,"E40.bottom"),sQuery(id+"F60.wireOp",EDGE,"E40.top"),sQuery(id+"F60.wireOp",EDGE,"E40.right")])],"isStart":true});
            var sketch = newSketch(context, id + "F64", { "sketchPlane" : qUnion([Q0])});
            skCircle(sketch, "E43.cCircle", {"center": v(-148.54, 0) * mm, "radius": 15.42 * mm, "construction": true});
            skLineSegment(sketch, "E43.0", {"start": v(-157.64, 14) * mm, "end": v(-145.08, 16.33) * mm});
            skLineSegment(sketch, "E43.1", {"start": v(-145.08, 16.33) * mm, "end": v(-134.55, 9.1) * mm});
            skLineSegment(sketch, "E43.2", {"start": v(-134.55, 9.1) * mm, "end": v(-132.21, -3.47) * mm});
            skLineSegment(sketch, "E43.3", {"start": v(-132.21, -3.47) * mm, "end": v(-139.45, -14) * mm});
            skLineSegment(sketch, "E43.4", {"start": v(-139.45, -14) * mm, "end": v(-152, -16.33) * mm});
            skLineSegment(sketch, "E43.5", {"start": v(-152, -16.33) * mm, "end": v(-162.54, -9.1) * mm});
            skLineSegment(sketch, "E43.6", {"start": v(-162.54, -9.1) * mm, "end": v(-164.87, 3.47) * mm});
            skLineSegment(sketch, "E43.7", {"start": v(-164.87, 3.47) * mm, "end": v(-157.64, 14) * mm});
            skPoint(sketch, "E43.0.midPoint", {"position": v(-151.36, 15.16) * mm});
            skSolve(sketch);
        }
        {
            var Q0;
            Q0 = qSketchRegion(id + "F64", true);
            extrude(context, id + "F65", {"entities" : qUnion([Q0]), "operationType" : NewBodyOperationType.ADD, "depth" : 235.46 * mm, "offsetDistance" : 25.4 * mm});
        }
        {
            var Q0;
            Q0=makeQuery(id+"F65.opExtrude","CAP_FACE",FACE,{"disambiguationData":[OSD([sQuery(id+"F64.wireOp",EDGE,"E43.0"),sQuery(id+"F64.wireOp",EDGE,"E43.1"),sQuery(id+"F64.wireOp",EDGE,"E43.2"),sQuery(id+"F64.wireOp",EDGE,"E43.3"),sQuery(id+"F64.wireOp",EDGE,"E43.4"),sQuery(id+"F64.wireOp",EDGE,"E43.5"),sQuery(id+"F64.wireOp",EDGE,"E43.6"),sQuery(id+"F64.wireOp",EDGE,"E43.7")])],"isStart":false});
            cPlane(context, id + "F66", {"entities" : qUnion([Q0]), "cplaneType" : CPlaneType.OFFSET, "offset" : 0.76 * mm, "width" : 152.4 * mm, "height" : 152.4 * mm});
        }
        {
            var Q0;
            Q0=qCreatedBy(id+"F66.planeOp",FACE);
            var sketch = newSketch(context, id + "F67", { "sketchPlane" : qUnion([Q0])});
            skCircle(sketch, "E44", {"center": v(-148.75, 0) * mm, "radius": 28.12 * mm});
            skSolve(sketch);
        }
        {
            var Q0;
            Q0 = qSketchRegion(id + "F67", true);
            extrude(context, id + "F68", {"entities" : qUnion([Q0]), "depth" : 7.62 * mm, "offsetDistance" : 25.4 * mm});
        }
        {
            var Q0;
            Q0=makeQuery(id+"F68.opExtrude","CAP_FACE",FACE,{"disambiguationData":[OSD([sQuery(id+"F67.wireOp",EDGE,"E44")])],"isStart":false});
            cPlane(context, id + "F69", {"entities" : qUnion([Q0]), "cplaneType" : CPlaneType.OFFSET, "offset" : 0.2 * mm, "width" : 152.4 * mm, "height" : 152.4 * mm});
        }
        {
            var Q0;
            Q0=qCreatedBy(id+"F69.planeOp",FACE);
            var sketch = newSketch(context, id + "F70", { "sketchPlane" : qUnion([Q0])});
            skLineSegment(sketch, "E45.bottom", {"start": v(-166.66, 17.48) * mm, "end": v(-131.61, 17.48) * mm});
            skLineSegment(sketch, "E45.top", {"start": v(-166.66, -16.72) * mm, "end": v(-131.61, -16.72) * mm});
            skLineSegment(sketch, "E45.left", {"start": v(-166.66, 17.48) * mm, "end": v(-166.66, -16.72) * mm});
            skLineSegment(sketch, "E45.right", {"start": v(-131.61, 17.48) * mm, "end": v(-131.61, -16.72) * mm});
            skSolve(sketch);
        }
        {
            var Q0;
            Q0 = qSketchRegion(id + "F70", true);
            extrude(context, id + "F71", {"entities" : qUnion([Q0]), "depth" : 28.7 * mm, "offsetDistance" : 25.4 * mm});
        }
        {
            var Q0;
            Q0=makeQuery(id+"F71.opExtrude","SWEPT_FACE",FACE,{"disambiguationData":[OSD([sQuery(id+"F70.wireOp",EDGE,"E45.top")])]});
            var sketch = newSketch(context, id + "F72", { "sketchPlane" : qUnion([Q0])});
            skLineSegment(sketch, "E46", {"start": v(-149.14, 293.86) * mm, "end": v(-166.66, 272.75) * mm});
            skPoint(sketch, "E46.startSnap0", {"position": v(-149.14, 272.75) * mm});
            skLineSegment(sketch, "E47", {"start": v(-166.66, 272.75) * mm, "end": v(-131.61, 272.75) * mm});
            skLineSegment(sketch, "E48", {"start": v(-131.61, 272.75) * mm, "end": v(-149.14, 293.86) * mm});
            skSolve(sketch);
        }
        {
            var Q0;
            Q0=makeQuery(id+"F72.imprint","IMPRINT",FACE,{"disambiguationData":[TD([[makeQuery(id+"F72.imprint","IMPRINT",EDGE,{"derivedFrom":sQuery(id+"F72.wireOp",EDGE,"E46")}),1.0]])]});
            extrude(context, id + "F73", {"entities" : qUnion([Q0]), "operationType" : NewBodyOperationType.ADD, "oppositeDirection" : true, "depth" : 34.37 * mm, "offsetDistance" : 25.4 * mm});
        }
        {
            var Q0;
            Q0=makeQuery(id+"F73.boolean.opBoolean","MERGE",FACE,{"derivedFrom":[makeQuery(id+"F71.opExtrude","SWEPT_FACE",FACE,{"disambiguationData":[OSD([sQuery(id+"F70.wireOp",EDGE,"E45.top")])]}),makeQuery(id+"F73.opExtrude","CAP_FACE",FACE,{"disambiguationData":[OSD([sQuery(id+"F72.wireOp",EDGE,"E46"),sQuery(id+"F72.wireOp",EDGE,"E47"),sQuery(id+"F72.wireOp",EDGE,"E48")])],"isStart":true})]});
            var sketch = newSketch(context, id + "F74", { "sketchPlane" : qUnion([Q0])});
            skLineSegment(sketch, "E49.bottom", {"start": v(-161.82, 268.99) * mm, "end": v(-152.34, 268.99) * mm});
            skLineSegment(sketch, "E49.top", {"start": v(-161.82, 259.9) * mm, "end": v(-152.34, 259.9) * mm});
            skLineSegment(sketch, "E49.left", {"start": v(-161.82, 268.99) * mm, "end": v(-161.82, 259.9) * mm});
            skLineSegment(sketch, "E49.right", {"start": v(-152.34, 268.99) * mm, "end": v(-152.34, 259.9) * mm});
            skLineSegment(sketch, "E50.bottom", {"start": v(-145.48, 268.99) * mm, "end": v(-136.06, 268.99) * mm});
            skLineSegment(sketch, "E50.top", {"start": v(-145.48, 259.9) * mm, "end": v(-136.06, 259.9) * mm});
            skLineSegment(sketch, "E50.left", {"start": v(-145.48, 268.99) * mm, "end": v(-145.48, 259.9) * mm});
            skLineSegment(sketch, "E50.right", {"start": v(-136.06, 268.99) * mm, "end": v(-136.06, 259.9) * mm});
            skSolve(sketch);
        }
        {
            var Q0;
            Q0=makeQuery(id+"F74.imprint","IMPRINT",FACE,{"disambiguationData":[TD([[makeQuery(id+"F74.imprint","IMPRINT",EDGE,{"derivedFrom":sQuery(id+"F74.wireOp",EDGE,"E49.bottom")}),-1.0]])]});
            var Q1;
            Q1=makeQuery(id+"F74.imprint","IMPRINT",FACE,{"disambiguationData":[TD([[makeQuery(id+"F74.imprint","IMPRINT",EDGE,{"derivedFrom":sQuery(id+"F74.wireOp",EDGE,"E50.bottom")}),-1.0]])]});
            extrude(context, id + "F75", {"entities" : qUnion([Q0, Q1]), "operationType" : NewBodyOperationType.REMOVE, "oppositeDirection" : true, "depth" : 1.47 * mm, "offsetDistance" : 25.4 * mm});
        }
    });
